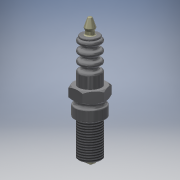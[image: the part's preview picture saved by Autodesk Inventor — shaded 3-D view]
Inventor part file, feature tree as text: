
AUTODESK INVENTOR PART (.ipt)
format: ipt  version: 2018 (Build 220112000, 112)  size: 455,680 bytes
history: native  units: mm
features: sketch x9, extrude x4, revolve x3, fillet x2, projected_geometry x2, plane x1, sweep x1, thread x1
ambient origin geometry x8: Origin, YZ Plane, XZ Plane, XY Plane, X Axis, Y Axis, Z Axis, Center Point
bodies: Solid1 (feature_tree), Solid2 (feature_tree), Solid3 (feature_tree)
feature tree (23):
  revolve  "Revolution1"  [1 undecoded]
  revolve  "Revolution2"  [1 undecoded]
  plane  "Work Plane1"
  extrude  "Extrusion1"  Depth=0.25mm
  revolve  "Revolution3"  [1 undecoded]
  extrude  "Extrusion2"  Depth=2.0mm
  extrude  "Extrusion3"  TaperAngle=90.0deg  [1 undecoded]
  extrude  "Extrusion4"  Depth=0.25mm
  sweep  "Sweep1"
  fillet  "Fillet1"  Radius=0.9mm
  fillet  "Fillet2"  Radius=11.419689mm
  thread  "Thread1"  [1 undecoded]
  sketch  "Sketch1"  dims[d0=17.5mm d1=2.0mm]
  sketch  "Sketch2"  dims[d2=1.0mm d3=60.0mm d5=1.0mm d6=10.0mm d8=10.0mm]
  sketch  "Sketch3"  dims[d10=20.0mm d12=1.0mm d13=10.0mm d15=10.0mm d17=0.25mm]
  sketch  "Sketch4"  dims[d18=0.25mm d19=1.75mm]
  sketch  "Sketch5"  dims[d20=0.04mm d21=2.0mm]
  sketch  "Sketch6"  dims[d22=7.0mm d23=90.0deg]
  sketch  "Sketch7"  dims[d24=0.083mm d25=0.25mm]
  sketch  "Sketch8"  dims[d26=2.125mm d27=3.42mm d28=0.9mm d29=11.419689mm d30=3.413864mm]
  projected_geometry  "Projected Loop1"
  sketch  "Sketch9"  dims[d31=2.01mm d32=0.25mm d33=0.620228mm d34=90.0deg d35=-14.0mm d36=3.9mm d37=2.4mm d38=0.0mm d39=11.0mm d40=1.2mm d41=3.35mm d43=0.25mm d44=90.0deg d45=4100.0mm d46=0.0mm d47=100.0mm d48=60.0deg d49=25.0mm d50=50.0mm d51=60.0deg d52=0.0mm d53=0.5mm d54=1.4mm d55=1.0mm d56=0.0mm d57=1.0mm d58=3.0mm d59=8.0mm d60=8.0mm d61=0.0mm d62=0.0mm d63=0.15mm d64=0.25mm d65=10.0mm d66=0.0mm]
  projected_geometry  "Project Cut Edges1"
note: 5 required parameter values undecoded (feature->parameter linkage not recoverable at this tier; creation-order binding heuristic only, values carry confidence <= 0.55)